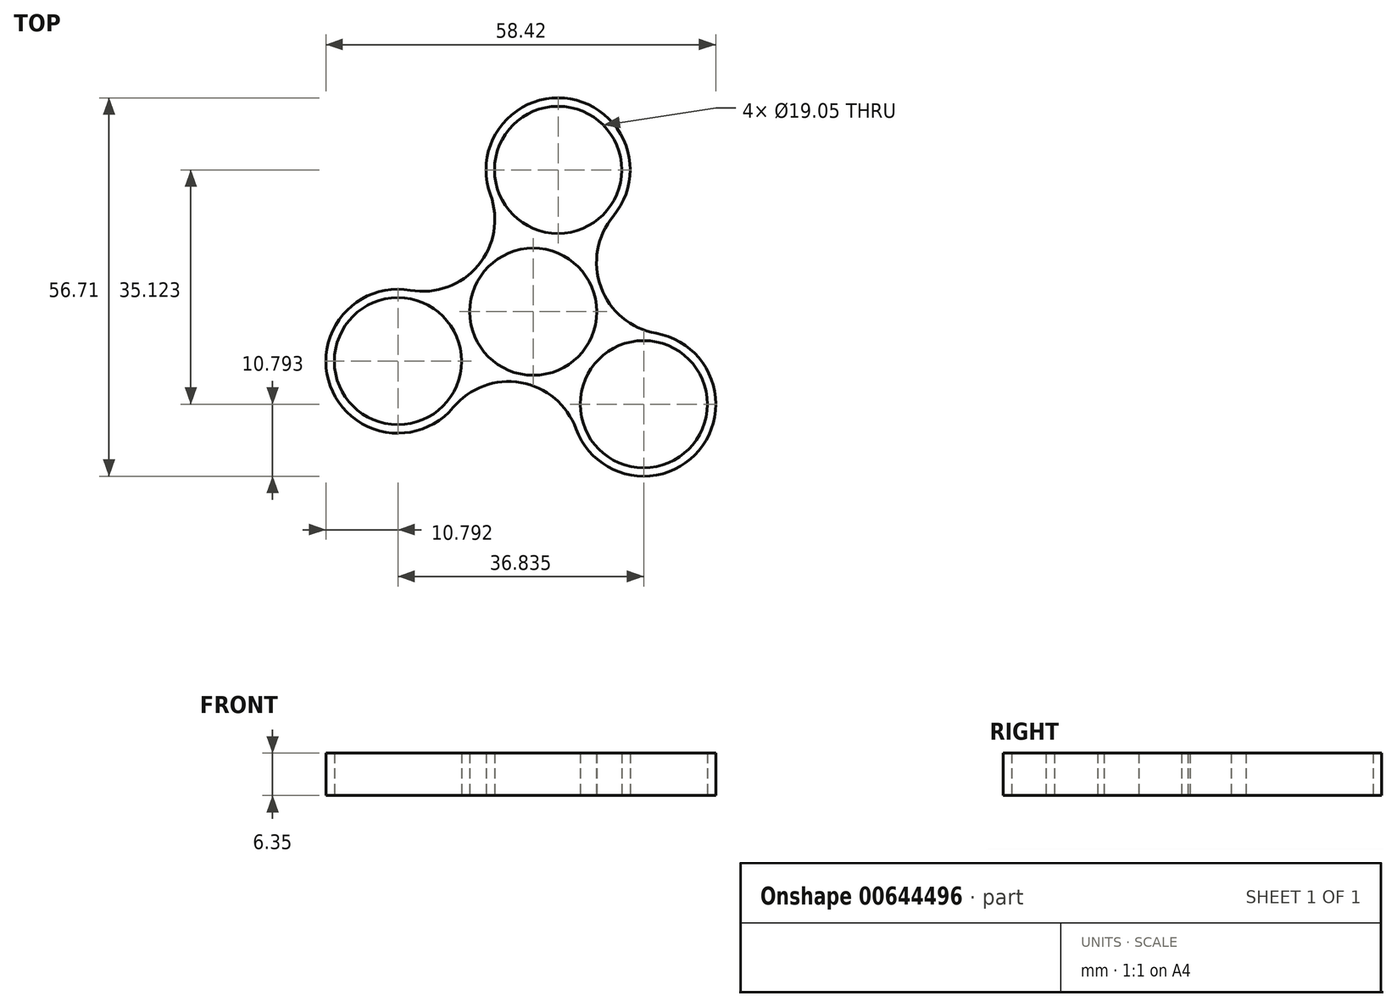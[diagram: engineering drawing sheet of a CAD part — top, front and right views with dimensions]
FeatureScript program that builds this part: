
annotation { "Feature Type Name" : "Feature", "Feature Type Description" : "" }
export const myFeature = defineFeature(function(context is Context, id is Id, definition is map)
    precondition{}
    {
        {
            var Q0;
            Q0=qCreatedBy(makeId("Top.planeOp"),FACE);
            var sketch = newSketch(context, id + "F0", { "sketchPlane" : qUnion([Q0])});
            skCircle(sketch, "E0", {"center": v(0, 0) * mm, "radius": 9.53 * mm});
            skArc(sketch, "E1", {"start": v(-18.42, 3.22) * mm, "mid": v(-8.28, 6.93) * mm, "end": v(-6.42, 17.56) * mm});
            skArc(sketch, "E2", {"start": v(12, 14.34) * mm, "mid": v(5.58, 31.9) * mm, "end": v(-6.42, 17.56) * mm});
            skArc(sketch, "E3", {"start": v(12, 14.34) * mm, "mid": v(10.14, 3.7) * mm, "end": v(18.42, -3.22) * mm});
            skArc(sketch, "E4", {"start": v(-18.42, 3.22) * mm, "mid": v(-30.42, -11.12) * mm, "end": v(-12, -14.34) * mm});
            skArc(sketch, "E5", {"start": v(6.42, -17.56) * mm, "mid": v(-1.86, -10.63) * mm, "end": v(-12, -14.34) * mm});
            skArc(sketch, "E6", {"start": v(6.42, -17.56) * mm, "mid": v(24.84, -20.78) * mm, "end": v(18.42, -3.22) * mm});
            skCircle(sketch, "E7", {"center": v(-20.28, -7.41) * mm, "radius": 9.53 * mm});
            skCircle(sketch, "E8", {"center": v(3.72, 21.27) * mm, "radius": 9.53 * mm});
            skCircle(sketch, "E9", {"center": v(16.56, -13.86) * mm, "radius": 9.53 * mm});
            skSolve(sketch);
        }
        {
            var Q0;
            Q0=makeQuery(id+"F0.imprint","IMPRINT",FACE,{"disambiguationData":[TD([[makeQuery(id+"F0.imprint","IMPRINT",EDGE,{"derivedFrom":sQuery(id+"F0.wireOp",EDGE,"E0")}),-1.0]])]});
            extrude(context, id + "F1", {"entities" : qUnion([Q0]), "depth" : 6.35 * mm, "offsetDistance" : 25.4 * mm});
        }
    });
